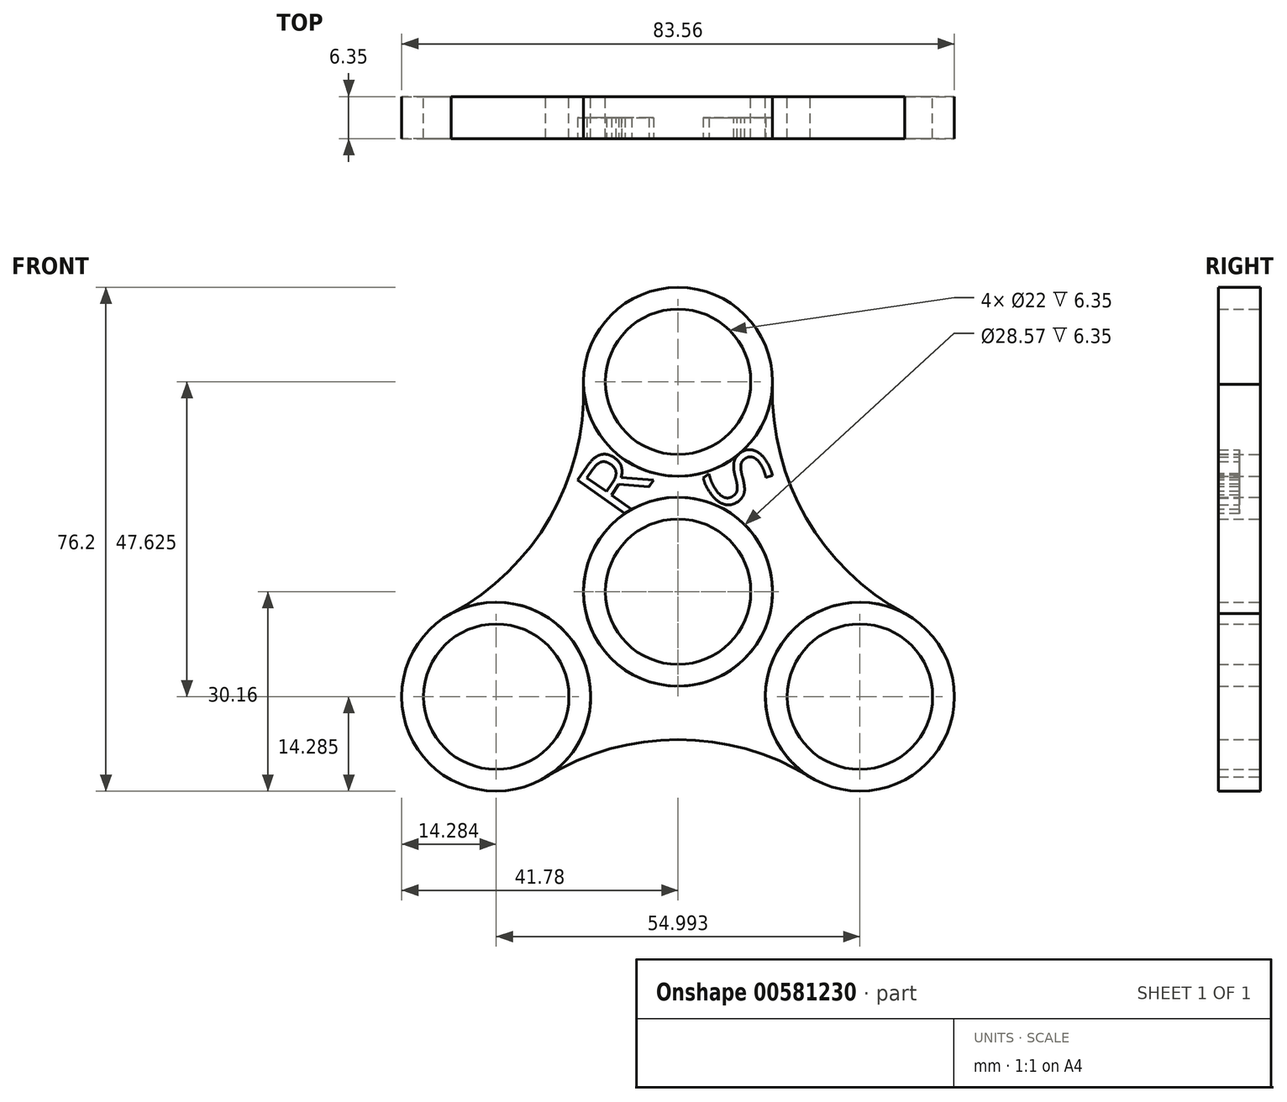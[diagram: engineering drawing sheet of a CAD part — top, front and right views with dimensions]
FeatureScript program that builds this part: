
annotation { "Feature Type Name" : "Feature", "Feature Type Description" : "" }
export const myFeature = defineFeature(function(context is Context, id is Id, definition is map)
    precondition{}
    {
        {
            var Q0;
            Q0=qCreatedBy(makeId("Front.planeOp"),FACE);
            var sketch = newSketch(context, id + "F0", { "sketchPlane" : qUnion([Q0])});
            skCircle(sketch, "E0", {"center": v(0, 0) * mm, "radius": 11 * mm});
            skCircle(sketch, "E1", {"center": v(0, 0) * mm, "radius": 14.29 * mm});
            skCircle(sketch, "E2", {"center": v(0, 31.75) * mm, "radius": 11 * mm});
            skCircle(sketch, "E3", {"center": v(0, 31.75) * mm, "radius": 14.29 * mm});
            skCircle(sketch, "E4.1.0", {"center": v(-27.5, -15.87) * mm, "radius": 11 * mm});
            skCircle(sketch, "E4.1.1", {"center": v(-27.5, -15.87) * mm, "radius": 14.29 * mm});
            skCircle(sketch, "E4.2.0", {"center": v(27.5, -15.88) * mm, "radius": 11 * mm});
            skCircle(sketch, "E4.2.1", {"center": v(27.5, -15.88) * mm, "radius": 14.29 * mm});
            skSolve(sketch);
        }
        {
            var Q0;
            Q0=makeQuery(id+"F0.imprint","IMPRINT",FACE,{"disambiguationData":[TD([[makeQuery(id+"F0.imprint","IMPRINT",EDGE,{"derivedFrom":sQuery(id+"F0.wireOp",EDGE,"E2")}),1.0]])]});
            var sketch = newSketch(context, id + "F1", { "sketchPlane" : qUnion([Q0])});
            skCircle(sketch, "E5.0", {"center": v(0, 31.75) * mm, "radius": 14.29 * mm});
            skCircle(sketch, "E6.0", {"center": v(-27.5, -15.87) * mm, "radius": 14.29 * mm});
            skArc(sketch, "E7", {"start": v(-34.28, -3.3) * mm, "mid": v(-19.37, 11.18) * mm, "end": v(-14.28, 31.34) * mm});
            skArc(sketch, "E8", {"start": v(14.28, 31.34) * mm, "mid": v(19.37, 11.18) * mm, "end": v(34.28, -3.3) * mm});
            skArc(sketch, "E9", {"start": v(20, -28.04) * mm, "mid": v(0, -22.37) * mm, "end": v(-20, -28.04) * mm});
            skCircle(sketch, "E10.0", {"center": v(27.5, -15.88) * mm, "radius": 14.29 * mm});
            skCircle(sketch, "E11.0", {"center": v(0, 0) * mm, "radius": 14.29 * mm});
            skSolve(sketch);
        }
        {
            var Q0;
            Q0=makeQuery(id+"F0.imprint","IMPRINT",FACE,{"disambiguationData":[TD([[makeQuery(id+"F0.imprint","IMPRINT",EDGE,{"derivedFrom":sQuery(id+"F0.wireOp",EDGE,"E2")}),-1.0]])]});
            var Q1;
            {var subQ0=sQuery(id+"F1.wireOp",EDGE,"E7");Q1=makeQuery(id+"F1.imprint","IMPRINT",FACE,{"disambiguationData":[TD([[makeQuery(id+"F1.imprint","IMPRINT",EDGE,{"derivedFrom":subQ0}),-1.0]])]});}
            var Q2;
            Q2=makeQuery(id+"F0.imprint","IMPRINT",FACE,{"disambiguationData":[TD([[makeQuery(id+"F0.imprint","IMPRINT",EDGE,{"derivedFrom":sQuery(id+"F0.wireOp",EDGE,"E4.1.0")}),-1.0]])]});
            var Q3;
            Q3=makeQuery(id+"F0.imprint","IMPRINT",FACE,{"disambiguationData":[TD([[makeQuery(id+"F0.imprint","IMPRINT",EDGE,{"derivedFrom":sQuery(id+"F0.wireOp",EDGE,"E0")}),-1.0]])]});
            var Q4;
            Q4=makeQuery(id+"F0.imprint","IMPRINT",FACE,{"disambiguationData":[TD([[makeQuery(id+"F0.imprint","IMPRINT",EDGE,{"derivedFrom":sQuery(id+"F0.wireOp",EDGE,"E4.2.0")}),-1.0]])]});
            extrude(context, id + "F2", {"entities" : qUnion([Q0, Q1, Q2, Q3, Q4]), "depth" : 6.35 * mm, "offsetDistance" : 25.4 * mm});
        }
        {
            var Q0;
            Q0=makeQuery(id+"F2.opExtrude","CAP_FACE",FACE,{"disambiguationData":[OSD([sQuery(id+"F1.wireOp",EDGE,"E5.0"),sQuery(id+"F1.wireOp",EDGE,"E6.0"),sQuery(id+"F1.wireOp",EDGE,"E7"),sQuery(id+"F1.wireOp",EDGE,"E8"),sQuery(id+"F1.wireOp",EDGE,"E9"),sQuery(id+"F1.wireOp",EDGE,"E10.0"),sQuery(id+"F1.wireOp",EDGE,"E11.0")])],"isStart":false});
            var sketch = newSketch(context, id + "F3", { "sketchPlane" : qUnion([Q0])});
            skText(sketch, "E12", { "text": "R", "fontName": "OpenSans-Regular.ttf"});
            skText(sketch, "E13", { "text": "S", "fontName": "OpenSans-Regular.ttf"});
            const initialGuessF3  = {"E12": [-0.00823, 0.0104, 0.57358, 0.81915, 0.00952], "E13": [0.00317, 0.0176, 0.57358, -0.81915, 0.00953]};
            skSetInitialGuess(sketch, initialGuessF3);
            skSolve(sketch);
        }
        {
            var Q0;
            {var subQ4=sQuery(id+"F3.wireOp",EDGE,"E12.sketch_text.stroke-3");Q0=makeQuery(id+"F3.imprint","IMPRINT",FACE,{"disambiguationData":[TD([[makeQuery(id+"F3.imprint","IMPRINT",EDGE,{"derivedFrom":subQ4}),-1.0]])]});}
            var Q1;
            Q1=makeQuery(id+"F3.imprint","IMPRINT",FACE,{"disambiguationData":[TD([[makeQuery(id+"F3.imprint","IMPRINT",EDGE,{"derivedFrom":sQuery(id+"F3.wireOp",EDGE,"E13.sketch_text.stroke-0")}),-1.0]])]});
            extrude(context, id + "F4", {"entities" : qUnion([Q0, Q1]), "operationType" : NewBodyOperationType.REMOVE, "oppositeDirection" : true, "depth" : 3.17 * mm, "offsetDistance" : 25.4 * mm});
        }
    });
